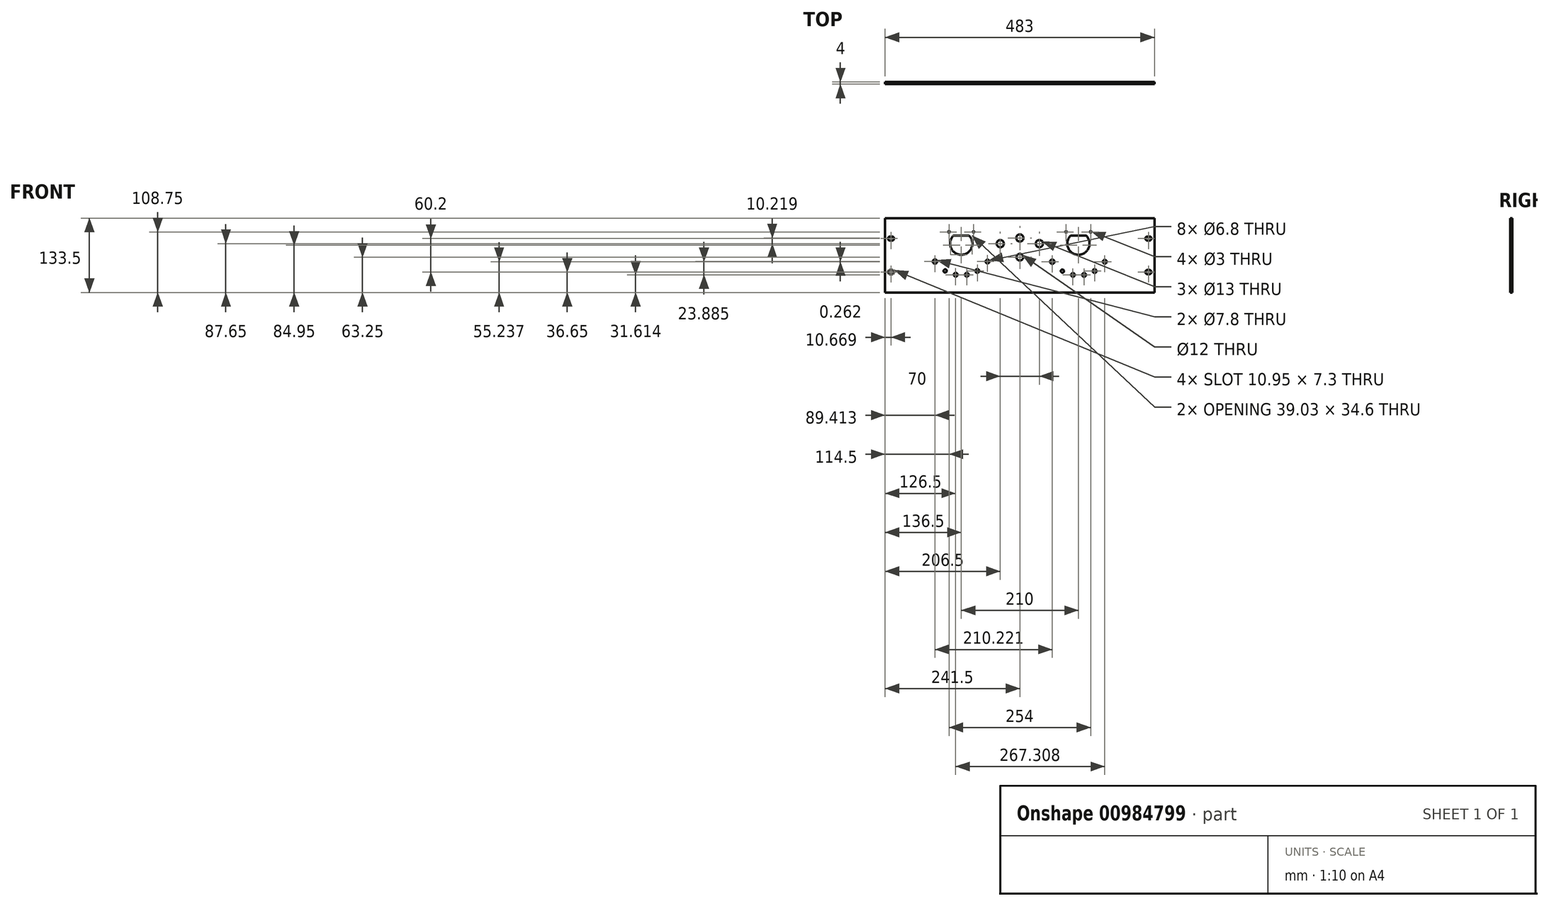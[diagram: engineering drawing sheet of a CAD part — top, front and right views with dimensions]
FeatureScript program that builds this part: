
annotation { "Feature Type Name" : "Feature", "Feature Type Description" : "" }
export const myFeature = defineFeature(function(context is Context, id is Id, definition is map)
    precondition{}
    {
        {
            var Q0;
            Q0=qCreatedBy(makeId("Front.planeOp"),FACE);
            var sketch = newSketch(context, id + "F0", { "sketchPlane" : qUnion([Q0])});
            skLineSegment(sketch, "E0.bottom", {"start": v(-241.5, 66.75) * mm, "end": v(241.5, 66.75) * mm});
            skLineSegment(sketch, "E0.top", {"start": v(-241.5, -66.75) * mm, "end": v(241.5, -66.75) * mm});
            skLineSegment(sketch, "E0.left", {"start": v(-241.5, 66.75) * mm, "end": v(-241.5, -66.75) * mm});
            skLineSegment(sketch, "E0.right", {"start": v(241.5, 66.75) * mm, "end": v(241.5, -66.75) * mm});
            skPoint(sketch, "E0.middle", {"position": v(0, 0) * mm});
            skArc(sketch, "E1", {"start": v(-229.02, -33.75) * mm, "mid": v(-225.36, -30.1) * mm, "end": v(-229.03, -26.45) * mm});
            skArc(sketch, "E2", {"start": v(-232.63, -26.45) * mm, "mid": v(-236.3, -30.09) * mm, "end": v(-232.66, -33.75) * mm});
            skLineSegment(sketch, "E3", {"start": v(-232.68, -26.45) * mm, "end": v(-228.98, -26.45) * mm});
            skLineSegment(sketch, "E4", {"start": v(-229, -33.75) * mm, "end": v(-232.66, -33.75) * mm});
            skArc(sketch, "E5", {"start": v(-229.03, 26.45) * mm, "mid": v(-225.36, 30.1) * mm, "end": v(-229.03, 33.75) * mm});
            skArc(sketch, "E6", {"start": v(-232.63, 33.75) * mm, "mid": v(-236.3, 30.11) * mm, "end": v(-232.66, 26.45) * mm});
            skLineSegment(sketch, "E7", {"start": v(-232.68, 33.75) * mm, "end": v(-228.98, 33.75) * mm});
            skLineSegment(sketch, "E8", {"start": v(-228.98, 26.45) * mm, "end": v(-232.66, 26.45) * mm});
            skArc(sketch, "E9", {"start": v(232.33, 26.45) * mm, "mid": v(236, 30.1) * mm, "end": v(232.33, 33.75) * mm});
            skArc(sketch, "E10", {"start": v(228.73, 33.75) * mm, "mid": v(225.06, 30.11) * mm, "end": v(228.7, 26.45) * mm});
            skLineSegment(sketch, "E11", {"start": v(228.68, 33.75) * mm, "end": v(232.38, 33.75) * mm});
            skLineSegment(sketch, "E12", {"start": v(232.38, 26.45) * mm, "end": v(228.7, 26.45) * mm});
            skArc(sketch, "E13", {"start": v(232.33, -33.75) * mm, "mid": v(236, -30.1) * mm, "end": v(232.33, -26.45) * mm});
            skArc(sketch, "E14", {"start": v(228.73, -26.45) * mm, "mid": v(225.06, -30.09) * mm, "end": v(228.7, -33.75) * mm});
            skLineSegment(sketch, "E15", {"start": v(228.68, -26.45) * mm, "end": v(232.38, -26.45) * mm});
            skLineSegment(sketch, "E16", {"start": v(232.38, -33.75) * mm, "end": v(228.7, -33.75) * mm});
            skLineSegment(sketch, "E17", {"start": v(-171.5, 66.75) * mm, "end": v(-171.5, -66.75) * mm, "construction": true});
            skLineSegment(sketch, "E18", {"start": v(171.5, 66.75) * mm, "end": v(171.5, -66.75) * mm, "construction": true});
            skLineSegment(sketch, "E19.bottom", {"start": v(-78.65, -2.5) * mm, "end": v(-131.35, -2.5) * mm, "construction": true});
            skLineSegment(sketch, "E19.top", {"start": v(-78.65, 46) * mm, "end": v(-131.35, 46) * mm, "construction": true});
            skLineSegment(sketch, "E19.left", {"start": v(-78.65, -2.5) * mm, "end": v(-78.65, 46) * mm, "construction": true});
            skLineSegment(sketch, "E19.right", {"start": v(-131.35, -2.5) * mm, "end": v(-131.35, 46) * mm, "construction": true});
            skPoint(sketch, "E19.middle", {"position": v(-105, 21.75) * mm});
            skLineSegment(sketch, "E20.bottom", {"start": v(131.35, -2.5) * mm, "end": v(78.65, -2.5) * mm, "construction": true});
            skLineSegment(sketch, "E20.top", {"start": v(131.35, 46) * mm, "end": v(78.65, 46) * mm, "construction": true});
            skLineSegment(sketch, "E20.left", {"start": v(131.35, -2.5) * mm, "end": v(131.35, 46) * mm, "construction": true});
            skLineSegment(sketch, "E20.right", {"start": v(78.65, -2.5) * mm, "end": v(78.65, 46) * mm, "construction": true});
            skPoint(sketch, "E20.middle", {"position": v(105, 21.75) * mm});
            skLineSegment(sketch, "E21.bottom", {"start": v(-9.5, -15.5) * mm, "end": v(9.5, -15.5) * mm, "construction": true});
            skLineSegment(sketch, "E21.top", {"start": v(-9.5, 15.5) * mm, "end": v(9.5, 15.5) * mm, "construction": true});
            skLineSegment(sketch, "E21.left", {"start": v(-9.5, -15.5) * mm, "end": v(-9.5, 15.5) * mm, "construction": true});
            skLineSegment(sketch, "E21.right", {"start": v(9.5, -15.5) * mm, "end": v(9.5, 15.5) * mm, "construction": true});
            skLineSegment(sketch, "E22", {"start": v(-9.5, 8.5) * mm, "end": v(9.5, 8.5) * mm, "construction": true});
            skCircle(sketch, "E23", {"center": v(0, -3.5) * mm, "radius": 6 * mm});
            skCircle(sketch, "E24", {"center": v(0, 31.12) * mm, "radius": 9.5 * mm, "construction": true});
            skCircle(sketch, "E25", {"center": v(0, 31.12) * mm, "radius": 6.5 * mm});
            skLineSegment(sketch, "E26", {"start": v(-241.5, 51.75) * mm, "end": v(241.5, 51.75) * mm, "construction": true});
            skLineSegment(sketch, "E27", {"start": v(-241.5, -51.75) * mm, "end": v(241.5, -51.75) * mm, "construction": true});
            skCircle(sketch, "E28", {"center": v(-152.09, -11.25) * mm, "radius": 13 * mm, "construction": true});
            skCircle(sketch, "E29", {"center": v(-133.8, -28.02) * mm, "radius": 5.5 * mm, "construction": true});
            skCircle(sketch, "E30", {"center": v(-115, -34.87) * mm, "radius": 5.5 * mm, "construction": true});
            skCircle(sketch, "E31", {"center": v(-95, -34.87) * mm, "radius": 5.5 * mm, "construction": true});
            skCircle(sketch, "E32", {"center": v(-76.2, -28.02) * mm, "radius": 5.5 * mm, "construction": true});
            skCircle(sketch, "E33", {"center": v(-105, 21.75) * mm, "radius": 57.5 * mm, "construction": true});
            skCircle(sketch, "E34", {"center": v(105, 21.75) * mm, "radius": 57.5 * mm, "construction": true});
            skCircle(sketch, "E35", {"center": v(-57.91, -11.25) * mm, "radius": 13 * mm, "construction": true});
            skCircle(sketch, "E36", {"center": v(35, 20.9) * mm, "radius": 9.5 * mm, "construction": true});
            skCircle(sketch, "E37", {"center": v(35, 20.9) * mm, "radius": 6.5 * mm});
            skCircle(sketch, "E38", {"center": v(-35, 20.9) * mm, "radius": 9.5 * mm, "construction": true});
            skCircle(sketch, "E39", {"center": v(-35, 20.9) * mm, "radius": 6.5 * mm});
            skCircle(sketch, "E40", {"center": v(-152.09, -11.25) * mm, "radius": 3.9 * mm});
            skCircle(sketch, "E41", {"center": v(-133.8, -28.02) * mm, "radius": 2.9 * mm});
            skCircle(sketch, "E42", {"center": v(-115, -34.87) * mm, "radius": 3.4 * mm});
            skCircle(sketch, "E43", {"center": v(-95, -34.87) * mm, "radius": 3.4 * mm});
            skCircle(sketch, "E44", {"center": v(-76.2, -28.02) * mm, "radius": 3.4 * mm});
            skCircle(sketch, "E45", {"center": v(-57.91, -11.25) * mm, "radius": 3.4 * mm});
            skArc(sketch, "E46", {"start": v(-118.67, 35.5) * mm, "mid": v(-105, 0.9) * mm, "end": v(-91.33, 35.5) * mm});
            skArc(sketch, "E47", {"start": v(91.33, 35.5) * mm, "mid": v(105, 0.9) * mm, "end": v(118.67, 35.5) * mm});
            skCircle(sketch, "E48", {"center": v(58.13, -11.51) * mm, "radius": 13 * mm, "construction": true});
            skCircle(sketch, "E49", {"center": v(76.43, -28.29) * mm, "radius": 5.5 * mm, "construction": true});
            skCircle(sketch, "E50", {"center": v(95.22, -35.14) * mm, "radius": 5.5 * mm, "construction": true});
            skCircle(sketch, "E51", {"center": v(115.22, -35.14) * mm, "radius": 5.5 * mm, "construction": true});
            skCircle(sketch, "E52", {"center": v(134.01, -28.29) * mm, "radius": 5.5 * mm, "construction": true});
            skCircle(sketch, "E53", {"center": v(152.3, -11.51) * mm, "radius": 13 * mm, "construction": true});
            skCircle(sketch, "E54", {"center": v(58.13, -11.51) * mm, "radius": 3.9 * mm});
            skCircle(sketch, "E55", {"center": v(76.43, -28.29) * mm, "radius": 2.9 * mm});
            skCircle(sketch, "E56", {"center": v(95.22, -35.14) * mm, "radius": 3.4 * mm});
            skCircle(sketch, "E57", {"center": v(115.22, -35.14) * mm, "radius": 3.4 * mm});
            skCircle(sketch, "E58", {"center": v(134.01, -28.29) * mm, "radius": 3.4 * mm});
            skCircle(sketch, "E59", {"center": v(152.3, -11.51) * mm, "radius": 3.4 * mm});
            skPoint(sketch, "E60", {"position": v(229.5, 54.75) * mm});
            skPoint(sketch, "E61", {"position": v(-229.5, -54.75) * mm});
            skPoint(sketch, "E62", {"position": v(-229.5, 54.75) * mm});
            skPoint(sketch, "E63", {"position": v(229.5, -54.75) * mm});
            skLineSegment(sketch, "E64", {"start": v(-118.67, 35.5) * mm, "end": v(-91.33, 35.5) * mm});
            skLineSegment(sketch, "E65", {"start": v(91.33, 35.5) * mm, "end": v(118.67, 35.5) * mm});
            skPoint(sketch, "E66.orphan", {"position": v(80.2, 35.5) * mm});
            skPoint(sketch, "E67.orphan", {"position": v(127.74, 35.5) * mm});
            skLineSegment(sketch, "E68", {"start": v(-166.01, 42) * mm, "end": v(-52.07, 42) * mm, "construction": true});
            skCircle(sketch, "E69", {"center": v(-127, 42) * mm, "radius": 1.5 * mm});
            skCircle(sketch, "E70", {"center": v(-83, 42) * mm, "radius": 1.5 * mm});
            skCircle(sketch, "E71", {"center": v(83, 42) * mm, "radius": 1.5 * mm});
            skCircle(sketch, "E72", {"center": v(127, 42) * mm, "radius": 1.5 * mm});
            skSolve(sketch);
        }
        {
            var Q0;
            Q0=makeQuery(id+"F0.imprint","IMPRINT",FACE,{"disambiguationData":[TD([[makeQuery(id+"F0.imprint","IMPRINT",EDGE,{"derivedFrom":sQuery(id+"F0.wireOp",EDGE,"E0.bottom")}),-1.0]])]});
            extrude(context, id + "F1", {"entities" : qUnion([Q0]), "depth" : 4 * mm, "offsetDistance" : 25 * mm});
        }
    });
